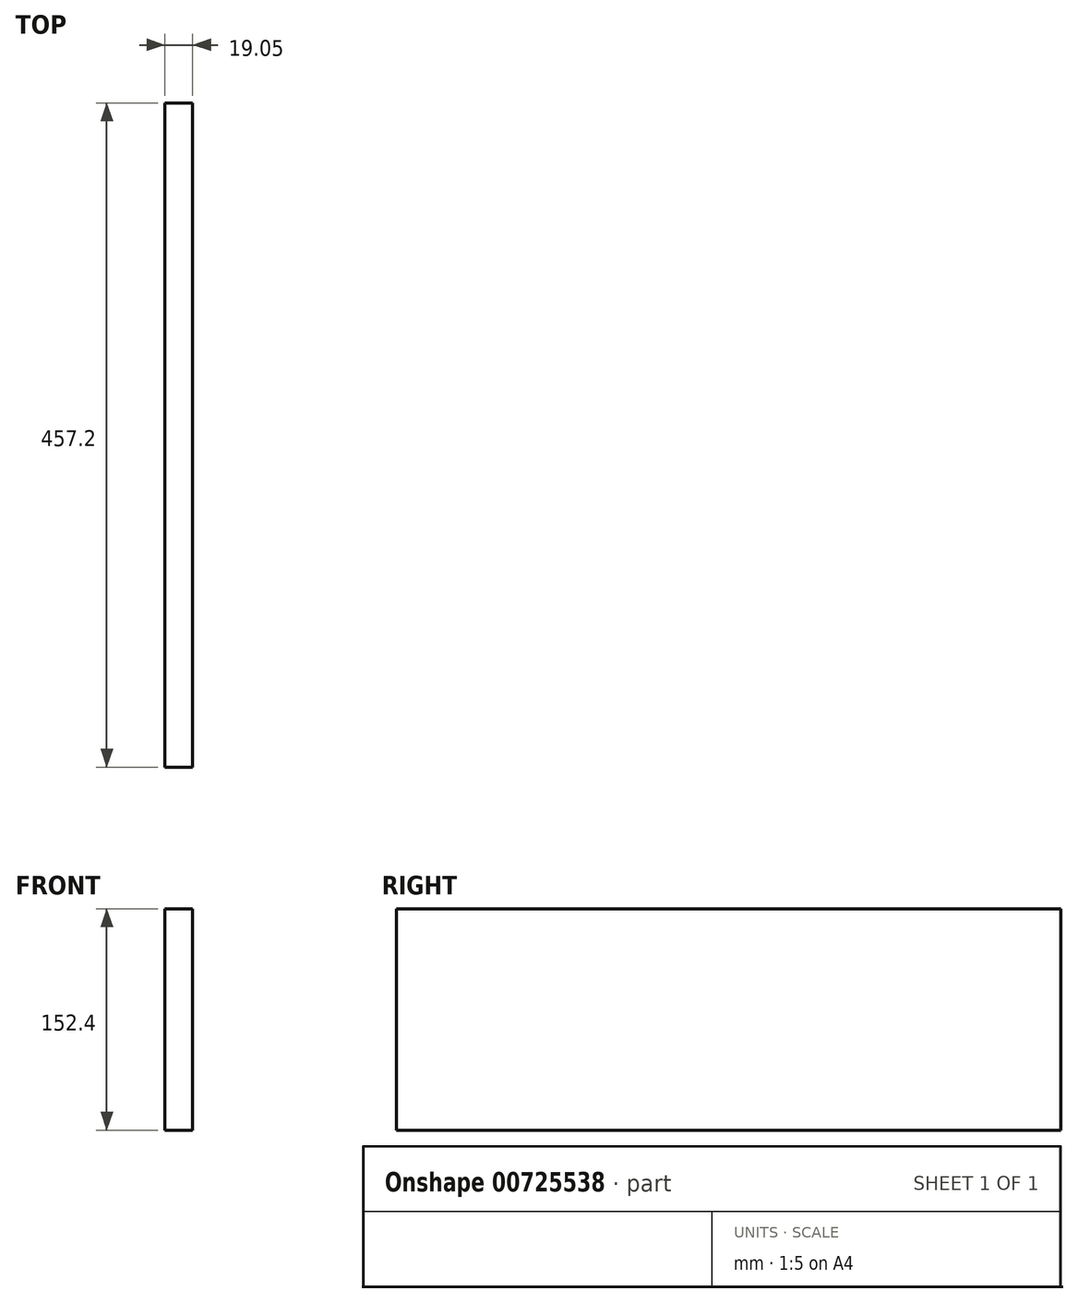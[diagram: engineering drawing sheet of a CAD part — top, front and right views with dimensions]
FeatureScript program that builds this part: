
annotation { "Feature Type Name" : "Feature", "Feature Type Description" : "" }
export const myFeature = defineFeature(function(context is Context, id is Id, definition is map)
    precondition{}
    {
        {
            var Q0;
            Q0=qCreatedBy(makeId("Right.planeOp"),FACE);
            var sketch = newSketch(context, id + "F0", { "sketchPlane" : qUnion([Q0])});
            skLineSegment(sketch, "E0.bottom", {"start": v(228.6, 76.2) * mm, "end": v(-228.6, 76.2) * mm});
            skLineSegment(sketch, "E0.top", {"start": v(228.6, -76.2) * mm, "end": v(-228.6, -76.2) * mm});
            skLineSegment(sketch, "E0.left", {"start": v(228.6, 76.2) * mm, "end": v(228.6, -76.2) * mm});
            skLineSegment(sketch, "E0.right", {"start": v(-228.6, 76.2) * mm, "end": v(-228.6, -76.2) * mm});
            skPoint(sketch, "E0.middle", {"position": v(0, 0) * mm});
            skSolve(sketch);
        }
        {
            var Q0;
            Q0=makeQuery(id+"F0.imprint","IMPRINT",FACE,{"disambiguationData":[TD([[makeQuery(id+"F0.imprint","IMPRINT",EDGE,{"derivedFrom":sQuery(id+"F0.wireOp",EDGE,"E0.bottom")}),1.0]])]});
            extrude(context, id + "F1", {"entities" : qUnion([Q0]), "depth" : 19.05 * mm, "offsetDistance" : 25.4 * mm});
        }
    });
